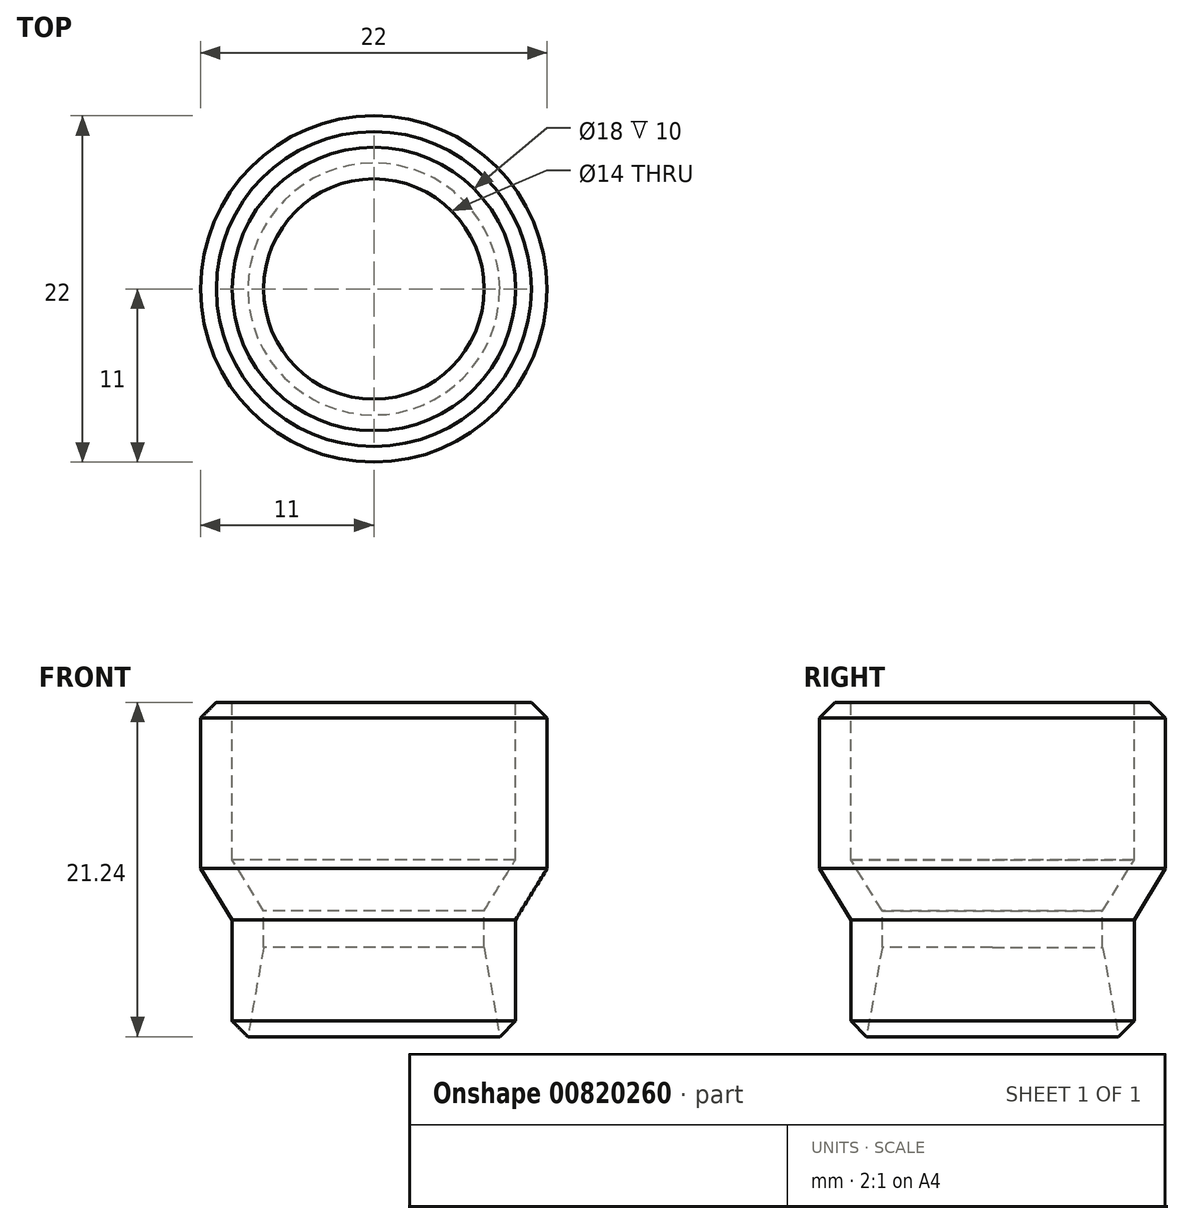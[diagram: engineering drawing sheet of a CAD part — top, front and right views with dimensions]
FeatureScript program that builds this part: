
annotation { "Feature Type Name" : "Feature", "Feature Type Description" : "" }
export const myFeature = defineFeature(function(context is Context, id is Id, definition is map)
    precondition{}
    {
        {
            var Q0;
            Q0=qCreatedBy(makeId("Front.planeOp"),FACE);
            var sketch = newSketch(context, id + "F0", { "sketchPlane" : qUnion([Q0])});
            skLineSegment(sketch, "E0", {"start": v(0, 4.45) * mm, "end": v(0, -6.9) * mm, "construction": true});
            skLineSegment(sketch, "E1", {"start": v(-9, 10) * mm, "end": v(-9, 0) * mm});
            skLineSegment(sketch, "E2", {"start": v(-7, -3.24) * mm, "end": v(-7, -11.24) * mm});
            skLineSegment(sketch, "E3", {"start": v(-9, 0) * mm, "end": v(-7, -3.24) * mm});
            skLineSegment(sketch, "E4.0", {"start": v(-11, 10) * mm, "end": v(-11, -0.6) * mm});
            skLineSegment(sketch, "E5.0", {"start": v(-11, -0.57) * mm, "end": v(-9, -3.81) * mm});
            skLineSegment(sketch, "E6.0", {"start": v(-9, -3.81) * mm, "end": v(-9, -11.24) * mm});
            skLineSegment(sketch, "E7", {"start": v(-11, 10) * mm, "end": v(-9, 10) * mm});
            skLineSegment(sketch, "E8", {"start": v(-9, -11.24) * mm, "end": v(-7, -11.24) * mm});
            skSolve(sketch);
        }
        {
            var Q0;
            Q0 = qSketchRegion(id + "F0", true);
            var Q1;
            Q1=sQuery(id+"F0.wireOp",EDGE,"E0");
            revolve(context, id + "F1", {"surfaceOperationType" : NewSurfaceOperationType.NEW, "entities" : qUnion([Q0]), "axis" : qUnion([Q1]), "revolveType" : RevolveType.FULL});
        }
        {
            var Q0;
            Q0=makeQuery(id+"F1.opRevolve","SWEPT_EDGE",EDGE,{"disambiguationData":[OSD([sQuery(id+"F0.wireOp",EDGE,"E6.0"),sQuery(id+"F0.wireOp",EDGE,"E8")])]});
            var Q1;
            Q1=makeQuery(id+"F1.opRevolve","SWEPT_EDGE",EDGE,{"disambiguationData":[OSD([sQuery(id+"F0.wireOp",EDGE,"E4.0"),sQuery(id+"F0.wireOp",EDGE,"E7")])]});
            chamfer(context, id + "F2", {"entities" : qUnion([Q0, Q1]), "chamferType" : ChamferType.OFFSET_ANGLE, "width" : 1 * mm, "oppositeDirection" : false, "angle" : 45 * degree, "tangentPropagation" : true});
        }
        {
            var Q0;
            Q0=makeQuery(id+"F1.opRevolve","SWEPT_EDGE",EDGE,{"disambiguationData":[OSD([sQuery(id+"F0.wireOp",EDGE,"E2"),sQuery(id+"F0.wireOp",EDGE,"E8")])]});
            chamfer(context, id + "F3", {"entities" : qUnion([Q0]), "chamferType" : ChamferType.OFFSET_ANGLE, "width" : 1 * mm, "oppositeDirection" : false, "angle" : 80 * degree, "tangentPropagation" : true});
        }
    });
